# Revit family: EU_SINGLE_ODU_Q_Ver.1.0
name_source: partatom
category: Mechanical Equipment
revit_build: Autodesk Revit 2016 (Build: 20150220_1215(x64)
units: mm (PartAtom-declared; Revit-internal decimal feet)

## family parameters
Always vertical = Yes
Cut with Voids When Loaded = No
Part Type = Normal
Room Calculation Point = No
Round Connector Dimension = Use Radius
Shared = No
Work Plane-Based = No

## types (8) — shared parameters
Designation = -
Fan Grill Diameter = 0.00 mm
Fan Grill Radius = 0.00 mm
Free Content Downloads = -
Location = -
Manufacturer = SAMSUNG
Manufacturer Metadata = -
Net Weight = 43.80 kg
Notes = -
Product Documentation Link = -
Product Page URL = -
Sales Rep Locator = -
Serial Number = -
Subscribe for Update Alerts = -
System Served = -
URL = www.samsung.com

## per-type parameters (varying)
| type | Model | Refrigerant Type |
| 5.00 kW, 220-240V, HEAT PUMP | AC052MXADKH/EU | R410A |
| 5.80 kW, 220-240V, HEAT PUMP | AC060MXADKH/EU | R410A |
| Single Heat Pump, 5.2kW, 220-240, R32, AC052RNNDKG/EU | AC052RXADKG/EU | R32 |
| Single Heat Pump, 5.2kW, 220-240, R32, AC052RN4DKG/EU | AC052RXADKG/EU | R32 |
| Single Heat Pump, 5.2kW, 220-240, R32, AC052RNLDKG/EU | AC052RXADKG/EU | R32 |
| Single Heat Pump, 5.2kW, 220-240, R32, AC052RNMDKG/EU | AC052RXADKG/EU | R32 |
| Single Heat Pump, 5.2kW, 220-240, R32, AC052RNADKG/EU | AC052RXADKG/EU | R32 |
| Single Heat Pump, 5.2kW, 220-240, R32, AC052RNCDKG/EU | AC052RXADKG/EU | R32 |

## geometry (parser evidence)
native form markers: Sweep x5
no freeform markers — native parametric forms only
